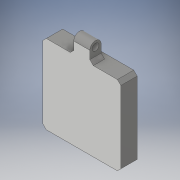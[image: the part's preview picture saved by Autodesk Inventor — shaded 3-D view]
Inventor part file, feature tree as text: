
AUTODESK INVENTOR PART (.ipt)
format: ipt  version: 2018 (Build 220112000, 112)  size: 375,808 bytes
history: native  units: in
note: dims shown in document units (in); Inventor stores cm internally (conversion verified against a paired STEP export)
features: extrude x3, sketch x3, move_body x2, chamfer x1, fillet x1, direct_edit x1
ambient origin geometry x8: Origin, YZ Plane, XZ Plane, XY Plane, X Axis, Y Axis, Z Axis, Center Point
bodies: Solid1 (feature_tree)
feature tree (11):
  extrude  "Extrusion1"  Depth=0.35in
  chamfer  "Chamfer1"  Distance=1.723in
  fillet  "Fillet1"  Radius=0.246in
  extrude  "Extrusion2"  Depth=0.11in TaperAngle=45.0deg
  extrude  "Extrusion3"  Depth=0.123in
  direct_edit  "Direct Edit1"
  sketch  "Sketch1"  dims[d0=0.35in d1=0.375in]
  sketch  "Sketch2"  dims[d2=0.57in]
  sketch  "Sketch4"  dims[d3=0.57in d4=1.723in d5=0.246in d6=0.0in d7=0.075in d8=0.125in d9=45.0deg d10=0.123in d11=0.146in d12=0.246in d13=0.0in d16=0.05in d17=0.125in d19=0.11in d20=0.0in d21=0.0in d22=0.0in d23=0.105in d24=0.0in d25=0.0in d26=0.105in]
  move_body  "Move1"
  move_body  "Move2"
